# Revit family: PGR_Noken_ShwrFitngsPckge_Rondo
name_source: partatom
category: Plumbing Fixtures
revit_build: Autodesk Revit 2017 (Build: 20171027_0315(x64)
units: mm (PartAtom-declared; Revit-internal decimal feet)

## family parameters
Always vertical = Yes
Cut with Voids When Loaded = No
Host = Wall
OmniClass Number = 23.45.05.14.17
OmniClass Title = Showers
Part Type = Normal
Room Calculation Point = No
Round Connector Dimension = Use Diameter
Shared = Yes

## types (1)
- Rondo-100106967
    AccessibilityPerformance = See ProductInformation for technical PDF
    AssetType = Fixed
    BIMObjectName = PGR_Noken_ShowerFittingsPackage_Rondo_Chrome-100106967
    BracketDescription = MINIMAL - Wall bracket with outlet elbow. Material brass, finish chrome plated, dimension 58 mm, nominal height 32 mm, net product weight 0,3 kg. EN-1112
    BracketInletConnectionSize = 1/2" G
    BracketNettWeight = 0.3
    BracketNominalLength = 78 mm
    BracketNominalWidth = 60 mm
    BracketNumberOfConnections = 2
    BracketOutletConnectionSize = 1/2" G
    BracketProductInformation = http://calidad.info-grupo.com:8081
    CWFU = 1
    Category = Pr_40_20_87_75: Shower fittings package
    CodePerformance = EN 1112, EN 248, EN 1111
    Collection = Rondo
    Color = Chrome
    Constituents = ShowerArm, ShowerHead, Valve, HandShower, Outlet, Flexihose
    Description = Rondo shower package
    DiameterCW = 15 mm
    DiameterHS = 15 mm  [stored 0.0492126 ft]
    DiameterHW = 15 mm
    DiameterSA = 15 mm  [stored 0.0492126 ft]
    DrainSize = 0 mm
    DurationUnit = year
    Features = See ProductInformation for technical PDF
    Finish = Chrome
    FlexiHoseDescription = 175 cm Flexi shower hose twist free. Material brass, finish chrome plated, dimension nominal 175 cm, net product weight 0,3 kg. Normative UNE EN 1113
    FlexiHoseInletConnectionSize = 1/2" G
    FlexiHoseNettWeight = 0.3
    FlexiHoseNominalLength = 1750 mm
    FlexiHoseNumberOfConnections = 2
    FlexiHoseOutletConnectionSize = 1/2" G
    FlexiHoseProductInformation = http://calidad.info-grupo.com:8081
    HandShowerDescription = MINIMAL - Single function handshower. Flow rate 13,26 l/min. at 3 bar. Material brass, finish chrome plated, dimension 207 mm, Ø 24 mm, net product weight 0,2 kg. Normative UNE EN 1112
    HandShowerFlowRate = 13 l./min.@3 bar
    HandShowerInletConnectionSize = 1/2" G
    HandShowerNettWeight = 0.2
    HandShowerNominalLength = 109 mm
    HandShowerNominalWidth = 24 mm
    HandShowerProductInformation = http://calidad.info-grupo.com:8081
    HasTray = No
    IfcExportAs = IfcSanitaryTerminalType
    IfcExportType = Shower
    ManufacturerURL = www.noken.com
    Material = Brass
    MaterialMetal = PGR_Noken_Brass_Chrome
    MaterialThickness = 0 mm  [stored 0 ft]
    Model = 100106967
    ModelNumber = 100106967
    ModelReference = Rondo shower package
    NBSDescription = Shower fittings package
    NBSReference = 45-35-70/330
    Name = ShowerFittingsPackage_Rondo_Chrome-100106967
    NominalDepth = 0 mm  [stored 0 ft]
    NominalHeight = 0 mm  [stored 0 ft]
    NominalLength = 0 mm  [stored 0 ft]
    NominalWidth = 0 mm  [stored 0 ft]
    ProductInformation = See any constituent's ProductInformation parameter for its own technical PDF
    Reference = -
    SAPBracket = 100039121
    SAPFlexihose = 100137893
    SAPHandShower = 100040325
    SAPShowerArm = 100063878
    SAPShowerHead = 100090355
    SAPValve = 100063403
    ShowerArmDescription = Oval 40 cm shower head arm, wall connection. Material brass, finish chrome plated, dimension 400 mm, nominal height 70 mm, net product weight 0,6 kg. Normative UNE EN 1112
    ShowerArmInletConnectionSize = 1/2" G
    ShowerArmNettWeight = 0.6
    ShowerArmNominalHeight = 70 mm
    ShowerArmNominalLength = 400 mm  [stored 1.31234 ft]
    ShowerArmNumberOfConnections = 2
    ShowerArmOutletConnectionSize = 1/2" G
    ShowerArmProductInformation = http://calidad.info-grupo.com:8081
    ShowerHeadDescription = Neptune slim Oval 30x20 cm rain shower head, with ball joint, with ball jointr. Material brass, finish chrome plated, dimension300x200 mm, nominal height 61 mm, net product weight 2,5 kg. Normative UNE EN 1112
    ShowerHeadFlowRate = Without flow regulator
    ShowerHeadInletConnectionSize = 1/2" G
    ShowerHeadNettWeight = 1.5
    ShowerHeadNominalLength = 300 mm
    ShowerHeadNominalWidth = 200 mm  [stored 0.656168 ft]
    ShowerHeadNumberOfConnections = 1
    ShowerHeadProductInformation = http://calidad.info-grupo.com:8081
    ShowerType = UNSET
    Status = UNSET
    SustainabilityPerformance = See ProductInformation for technical PDF
    TechnicalDrawing = See ProductInformation for technical PDF
    Type Image = 100106967.jpg
    URL = www.noken.com
    Uniclass2015Code = Pr_40_20_87_76
    Uniclass2015Title = Shower fittings package
    Uniclass2015Version = V1_8
    ValveDescription = Concealed thermostatic 2 ways 1/2"-3/4" with wax thermostatic element. Diverter valve with integrated shut off 1/2". Built in non-return valve. Safety stop at 38ºC. Flow rate bath 26 l/min. at 3 bar and flow rate shower 13 l/min.at 3 bar. 5 years warranty for superficial finishes and 2 years for the rest of components.
    ValveFlowRate = Flow rate bath 26 l/min. at 3 bar and flow rate shower 13 l/min.at 3 bar
    ValveInletConnectionSize = 3/4" G
    ValveNettWeight = 4.3
    ValveNominalDepth = 62-75
    ValveNominalLength = 200 mm  [stored 0.656168 ft]
    ValveNominalWidth = 150 mm  [stored 0.492126 ft]
    ValveNumberOfConnections = 4
    ValveOutletConnectionSize = 1/2" G
    ValveProductinformation = http://calidad.info-grupo.com:8081
    ValveType = Thermostatic
    Version = 1
    WarrantyDescription = See ProductInformation for technical PDF
    WarrantyDurationUnit = year

note: [stored X ft] marks values corroborated as IEEE doubles in the binary element streams (Revit-internal decimal feet)
